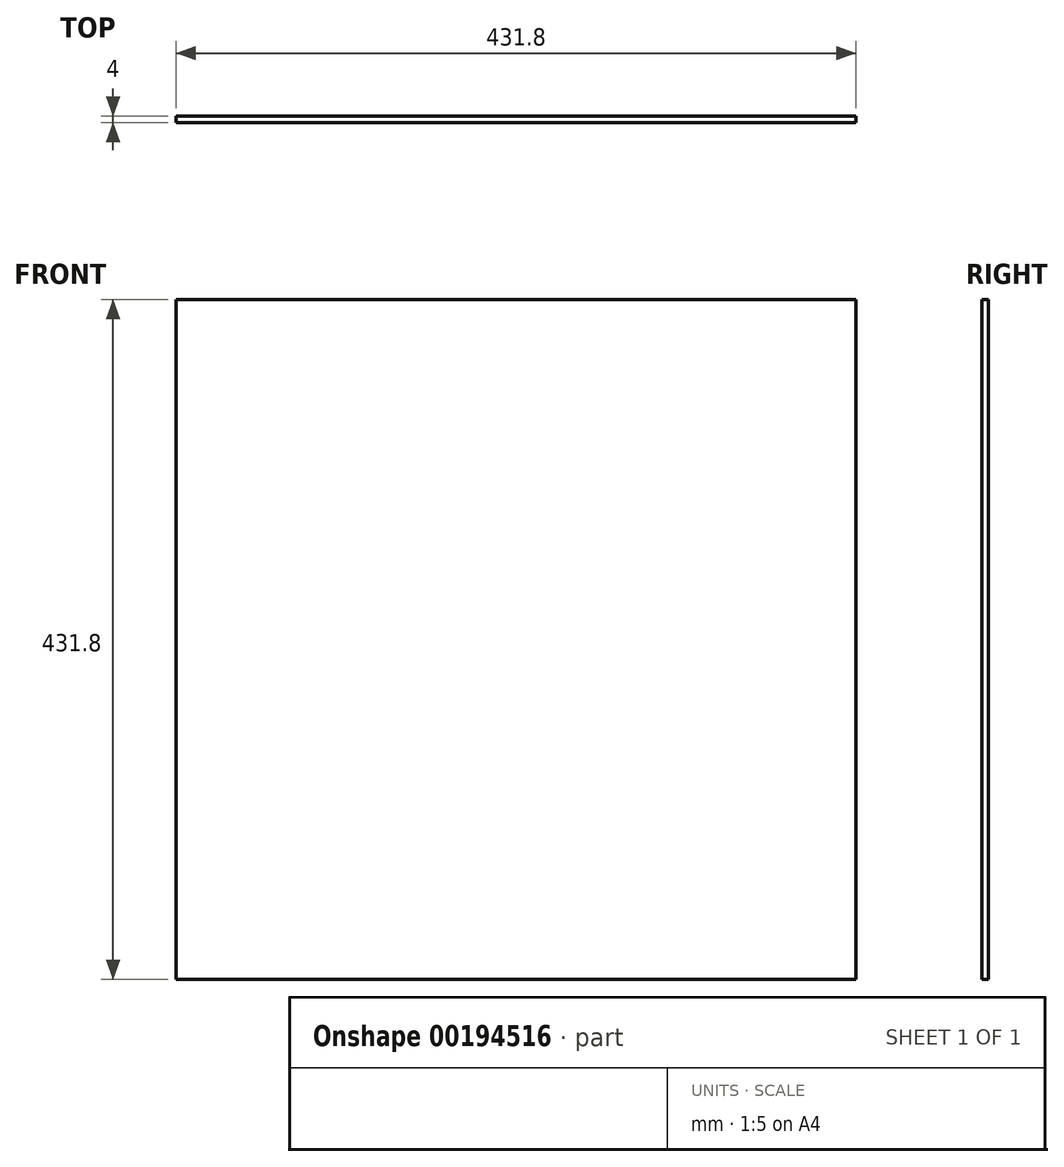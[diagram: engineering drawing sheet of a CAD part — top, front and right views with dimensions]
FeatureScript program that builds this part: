
annotation { "Feature Type Name" : "Feature", "Feature Type Description" : "" }
export const myFeature = defineFeature(function(context is Context, id is Id, definition is map)
    precondition{}
    {
        {
            var Q0;
            Q0=qCreatedBy(makeId("Front.planeOp"),FACE);
            var sketch = newSketch(context, id + "F0", { "sketchPlane" : qUnion([Q0])});
            skLineSegment(sketch, "E0.bottom", {"start": v(215.9, 215.9) * mm, "end": v(-215.9, 215.9) * mm});
            skLineSegment(sketch, "E0.top", {"start": v(215.9, -215.9) * mm, "end": v(-215.9, -215.9) * mm});
            skLineSegment(sketch, "E0.left", {"start": v(215.9, 215.9) * mm, "end": v(215.9, -215.9) * mm});
            skLineSegment(sketch, "E0.right", {"start": v(-215.9, 215.9) * mm, "end": v(-215.9, -215.9) * mm});
            skPoint(sketch, "E0.middle", {"position": v(0, 0) * mm});
            skSolve(sketch);
        }
        {
            var Q0;
            Q0=makeQuery(id+"F0.imprint","IMPRINT",FACE,{"disambiguationData":[TD([[makeQuery(id+"F0.imprint","IMPRINT",EDGE,{"derivedFrom":sQuery(id+"F0.wireOp",EDGE,"E0.bottom")}),1.0]])]});
            extrude(context, id + "F1", {"entities" : qUnion([Q0]), "depth" : 4 * mm, "offsetDistance" : 25.4 * mm});
        }
    });
